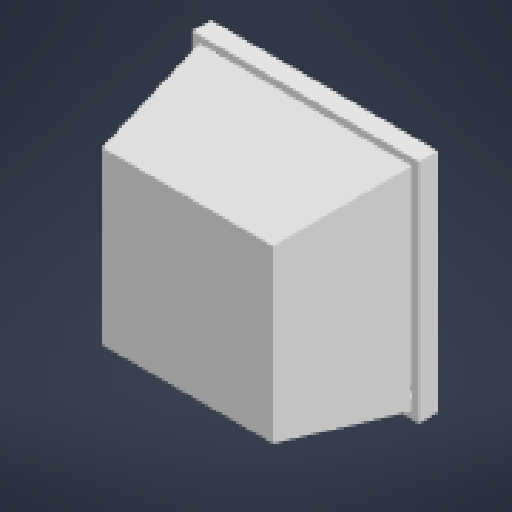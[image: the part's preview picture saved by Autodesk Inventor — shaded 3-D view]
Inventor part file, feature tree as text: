
AUTODESK INVENTOR PART (.ipt)
format: ipt  version: 2024.2 (Build 282272000, 272)  size: 141,312 bytes
history: native  units: mm
features: other x4, extrude x3, sketch x3, reference x2, projected_geometry x2
ambient origin geometry x8: Origin, YZ Plane, XZ Plane, XY Plane, X Axis, Y Axis, Z Axis, Center Point
bodies: Body1 (feature_tree)
feature tree (14):
  other  "솔리드1"
  extrude  "돌출1"  Depth=19.2mm
  extrude  "돌출2"  Depth=19.2mm
  extrude  "돌출3"  Depth=2.0mm
  sketch  "스케치1"
  reference  "참조1"
  reference  "참조2"
  sketch  "스케치2"
  projected_geometry  "투영된 루프1"
  sketch  "스케치3"
  projected_geometry  "투영된 루프2"
  other  "<userpath>\OneDrive\AAST\PART\AAST Remote Controler\AASTRC case.iam"
  other  "AASTRC case.iam"
  other  "AASTRC Bottom case:1"
